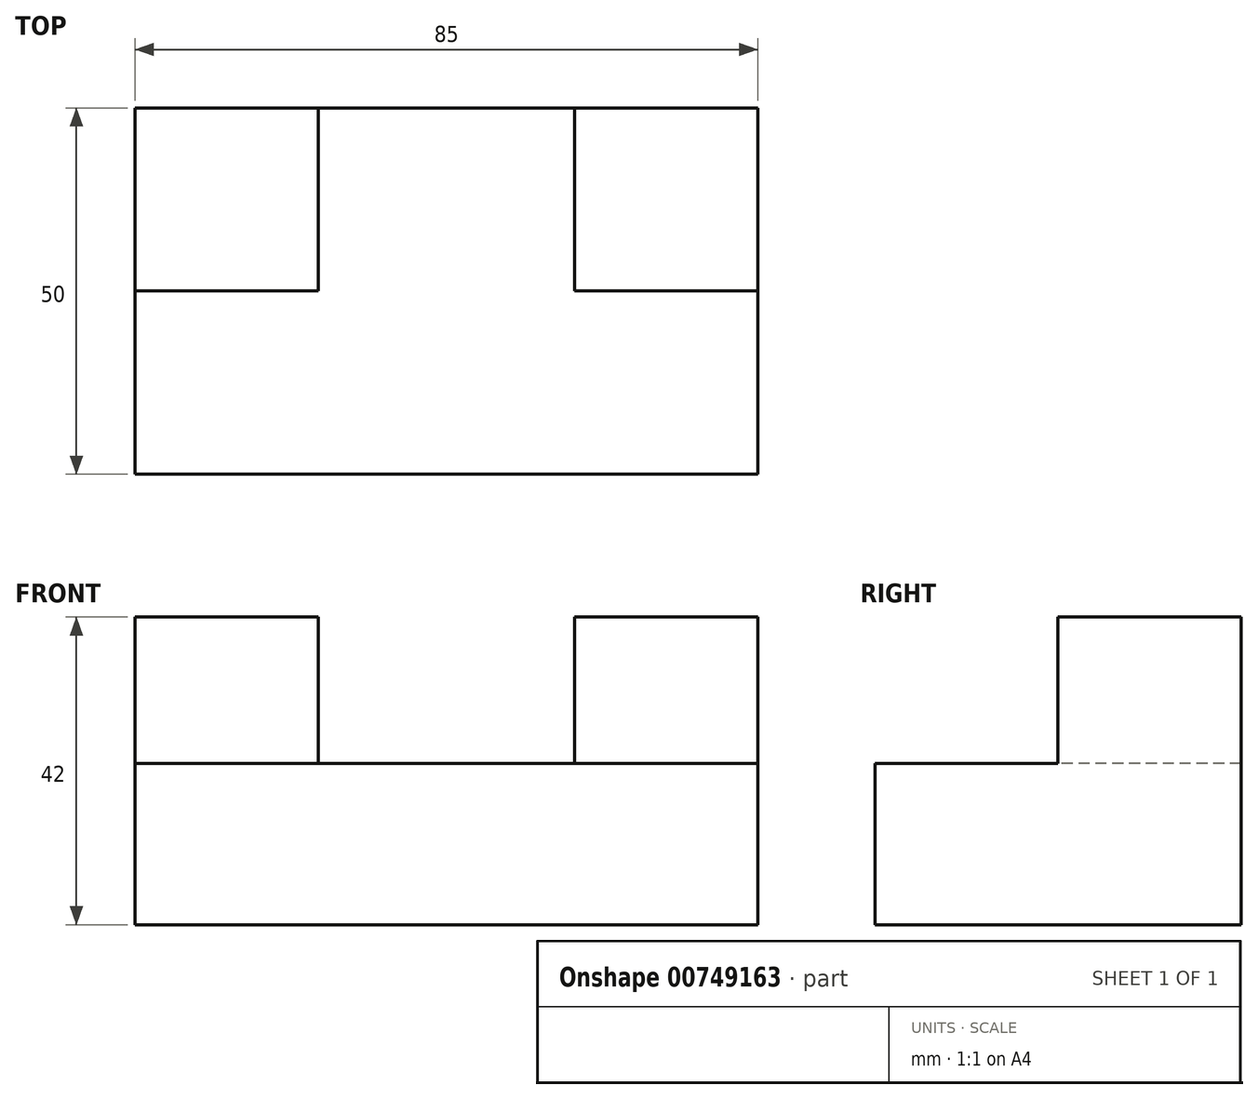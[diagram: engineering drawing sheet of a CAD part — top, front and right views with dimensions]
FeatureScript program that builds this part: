
annotation { "Feature Type Name" : "Feature", "Feature Type Description" : "" }
export const myFeature = defineFeature(function(context is Context, id is Id, definition is map)
    precondition{}
    {
        {
            var Q0;
            Q0=qCreatedBy(makeId("Front.planeOp"),FACE);
            var sketch = newSketch(context, id + "F0", { "sketchPlane" : qUnion([Q0])});
            skLineSegment(sketch, "E0", {"start": v(0, 0) * mm, "end": v(85, 0) * mm});
            skLineSegment(sketch, "E1", {"start": v(85, 0) * mm, "end": v(85, 22) * mm});
            skLineSegment(sketch, "E2", {"start": v(85, 22) * mm, "end": v(0, 22) * mm});
            skLineSegment(sketch, "E3", {"start": v(0, 22) * mm, "end": v(0, 0) * mm});
            skSolve(sketch);
        }
        {
            var Q0;
            Q0 = qSketchRegion(id + "F0", true);
            extrude(context, id + "F1", {"entities" : qUnion([Q0]), "depth" : 50 * mm, "offsetDistance" : 25 * mm});
        }
        {
            var Q0;
            Q0=makeQuery(id+"F1.opExtrude","SWEPT_FACE",FACE,{"disambiguationData":[OSD([sQuery(id+"F0.wireOp",EDGE,"E2")])]});
            var sketch = newSketch(context, id + "F2", { "sketchPlane" : qUnion([Q0])});
            skLineSegment(sketch, "E4", {"start": v(0, 0) * mm, "end": v(0, -25) * mm});
            skLineSegment(sketch, "E5", {"start": v(0, -25) * mm, "end": v(25, -25) * mm});
            skLineSegment(sketch, "E6", {"start": v(25, -25) * mm, "end": v(25, 0) * mm});
            skLineSegment(sketch, "E7", {"start": v(25, 0) * mm, "end": v(0, 0) * mm});
            skLineSegment(sketch, "E8", {"start": v(60, 0) * mm, "end": v(60, -25) * mm});
            skLineSegment(sketch, "E9", {"start": v(60, -25) * mm, "end": v(85, -25) * mm});
            skLineSegment(sketch, "E10", {"start": v(85, -25) * mm, "end": v(85, 0) * mm});
            skLineSegment(sketch, "E11", {"start": v(85, 0) * mm, "end": v(60, 0) * mm});
            skSolve(sketch);
        }
        {
            var Q0;
            Q0=makeQuery(id+"F2.imprint","IMPRINT",FACE,{"disambiguationData":[TD([[makeQuery(id+"F2.imprint","IMPRINT",EDGE,{"derivedFrom":sQuery(id+"F2.wireOp",EDGE,"E4")}),-1.0]])]});
            var Q1;
            Q1=makeQuery(id+"F2.imprint","IMPRINT",FACE,{"disambiguationData":[TD([[makeQuery(id+"F2.imprint","IMPRINT",EDGE,{"derivedFrom":sQuery(id+"F2.wireOp",EDGE,"E8")}),1.0]])]});
            extrude(context, id + "F3", {"entities" : qUnion([Q0, Q1]), "operationType" : NewBodyOperationType.ADD, "depth" : 20 * mm, "offsetDistance" : 25 * mm});
        }
    });
